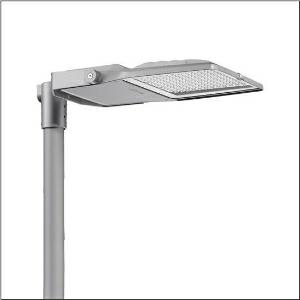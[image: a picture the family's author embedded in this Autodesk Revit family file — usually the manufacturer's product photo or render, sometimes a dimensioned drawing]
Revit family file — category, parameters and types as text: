
# Revit family: floodlight_fl_21_midi___pl52_5xa7786f2d3a_9b56
name_source: partatom
category: Lighting Fixtures
units: mm (PartAtom-declared; Revit-internal decimal feet)

## family parameters
Cut with Voids When Loaded = No
Host = Face
Light Source = No
Part Type = Normal
Room Calculation Point = No
Round Connector Dimension = Use Diameter
Shared = No

## types (1)
- --- (1 x LED, 35750 lm, 271.6 W, 3000K)
    Apparent Load = 272 VA
    CIE Flux Codes = 26 60 98 100 100
    Color Rendering = 70
    Color Temperature = 3000K
    Default Elevation = 1800 mm
    Description = Floodlight FL 21 midi, floodlight, primary light control with lens, of PMMA, primary optical cover: protective disc, of toughened safety glass, transparent, light distribution: PL52, light emission: direct distribution, installation type: surface-mounted, LED, High Power LED, rated luminous flux: 35.750lm, luminous efficacy: 132lm/W, light colour: 730, colour temperature: 3000K, control gear: Smart Interface (Zhaga), control: flexible luminous flux parameterisation, time-dependent luminous flux control, constant luminous flux control, overheat protection, pre-setting: logarithmic dimming characteristic, with terminal, 6-pole, mains connection: 220..240V, AC, 50/60Hz, start of lifetime: 272W, end of service life: 287W, reduction: 123W, luminaire housing, of diecast aluminium, powder-coated, SITECO metallic grey (DB 702S), corrosivity category C5 mid according to DIN EN ISO 12944, suitable for swimming pools, chlorine-resistant, sealing non-destructively replaceable, please order mast flange separately, mast bracket, of steel, galvanised, powder-coated, SITECO metallic grey (DB 702S), Smart Interface below and above, protection rating (complete): IP66, insulation class (complete): insulation class II (safety insulation), certification: CE, ENEC, VDE, protection symbol: D, impact resistance: IK08, permissible operating ambient temperature: -40..+40°C, permissible operating ambient temperature for outdoor applications: -40..+50°C, standard: DIN EN 12944, LABS conformity tested according to VDMA 24364:2018-05, packaging unit: 1 piece

Light Distribution: PL52
    Height = 76 mm
    Lamp = 1 x LED
    Lamp Light Flux = 35750 lm
    Lamp Power = 271.6 W
    Lamp count = 1
    Length = 657 mm
    Luminous efficacy = 132 lm/W
    Manufacturer = Siteco
    ModVariant = No
    Model = 5XA7786F2D3A
    Number of Poles = 1
    OnlyDefault = Yes
    Power Factor = 1
    Product Name = Floodlight FL 21 midi | PL52
    Product group = floodlight | pylon annexe
    ProductGroupID = 6201
    Protection Class = Protection class II
    Protection Degree = IP 66
    RLX_Detail_Level = 1
    RLX_Emergency_Light_Flux = 0 lm
    RLX_Emergency_Type = 0
    RLX_Emergency_Type_DB = No
    RlxData = <blob elided: 153845 chars, md5=c2f75a39>
    Socket = socket
    Standby Power = 0 W
    System Light Flux = 35750 lm
    System Power = 272 W
    Type Comments = factory setting: luminous flux: 100 % | dim-lin: 254 | 620 mA
    Type Image = l_1007123.jpg
    URL = http://relux.com
    VarID = @adj_176883
    Voltage = 0 V
    Weight = 0.00 kg
    Width = 442 mm

## geometry (parser evidence)
native form markers: Blend x4, Sweep x14
no freeform markers — native parametric forms only
